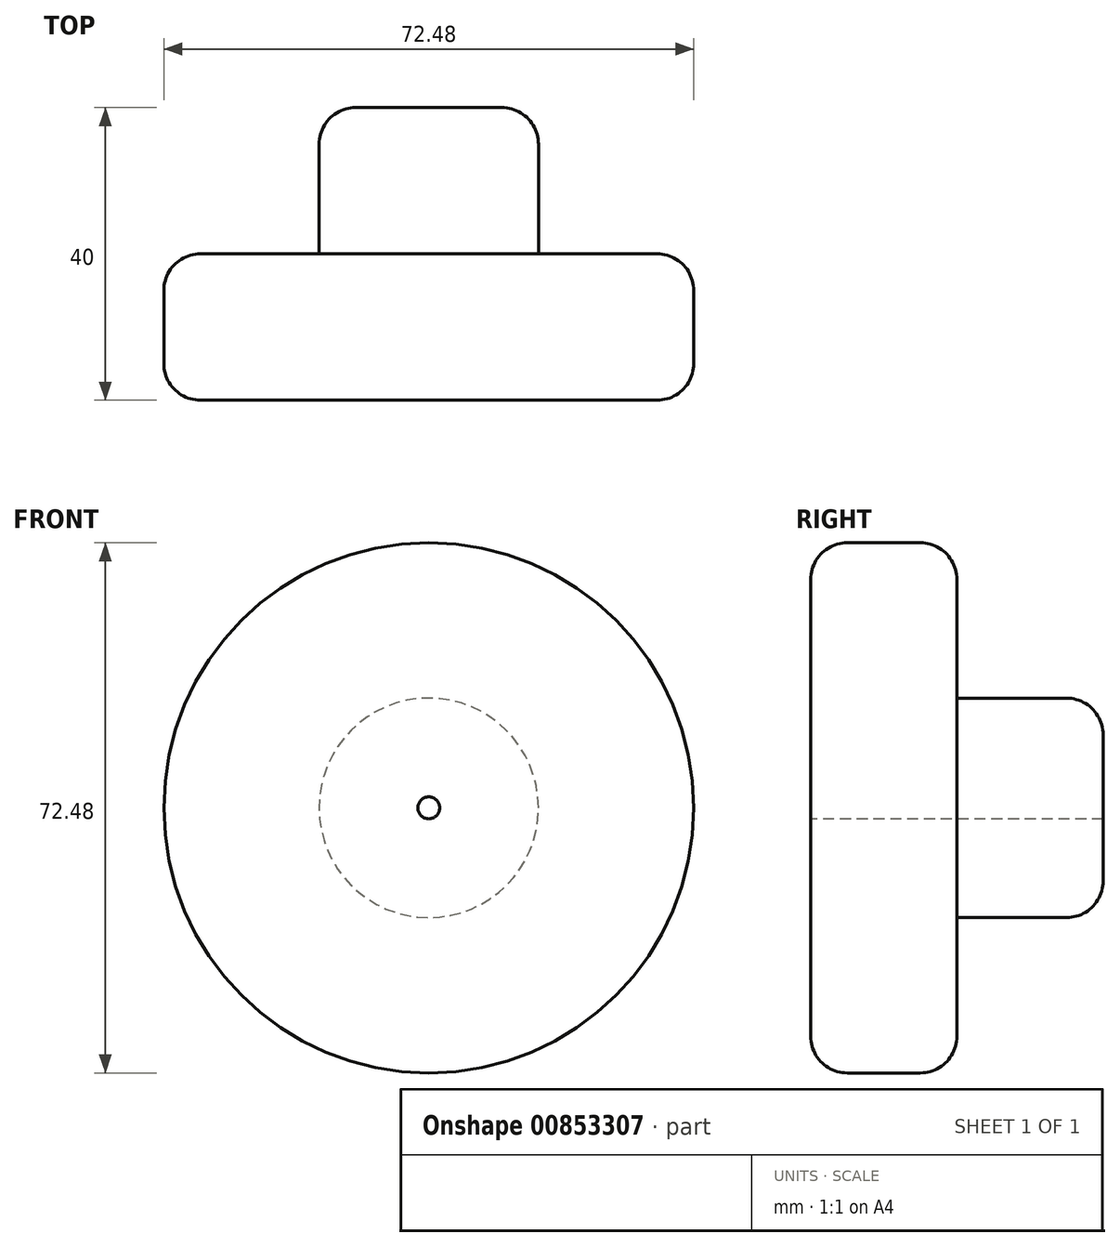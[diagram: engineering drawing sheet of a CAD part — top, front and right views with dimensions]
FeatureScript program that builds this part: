
annotation { "Feature Type Name" : "Feature", "Feature Type Description" : "" }
export const myFeature = defineFeature(function(context is Context, id is Id, definition is map)
    precondition{}
    {
        {
            var Q0;
            Q0=qCreatedBy(makeId("Top.planeOp"),FACE);
            var sketch = newSketch(context, id + "F0", { "sketchPlane" : qUnion([Q0])});
            skLineSegment(sketch, "E0", {"start": v(0, 0) * mm, "end": v(-15, 0) * mm});
            skLineSegment(sketch, "E1", {"start": v(-15, 0) * mm, "end": v(-15, -20) * mm});
            skLineSegment(sketch, "E2", {"start": v(-15, -20) * mm, "end": v(-36.24, -20) * mm});
            skLineSegment(sketch, "E3", {"start": v(-36.24, -20) * mm, "end": v(-36.24, -40) * mm});
            skLineSegment(sketch, "E4", {"start": v(-36.24, -40) * mm, "end": v(0, -40) * mm});
            skLineSegment(sketch, "E5", {"start": v(0, -40) * mm, "end": v(0, 0) * mm});
            skLineSegment(sketch, "E6", {"start": v(0, 30.53) * mm, "end": v(0, -53.97) * mm, "construction": true});
            skSolve(sketch);
        }
        {
            var Q0;
            Q0=makeQuery(id+"F0.imprint","IMPRINT",FACE,{"disambiguationData":[TD([[makeQuery(id+"F0.imprint","IMPRINT",EDGE,{"derivedFrom":sQuery(id+"F0.wireOp",EDGE,"E0")}),1.0]])]});
            var Q1;
            Q1=sQuery(id+"F0.wireOp",EDGE,"E6");
            revolve(context, id + "F1", {"surfaceOperationType" : NewSurfaceOperationType.NEW, "entities" : qUnion([Q0]), "axis" : qUnion([Q1]), "revolveType" : RevolveType.FULL});
        }
        {
            var Q0;
            Q0=makeQuery(id+"F1.opRevolve","SWEPT_EDGE",EDGE,{"disambiguationData":[OSD([sQuery(id+"F0.wireOp",EDGE,"E0"),sQuery(id+"F0.wireOp",EDGE,"E1")])]});
            var Q1;
            Q1=makeQuery(id+"F1.opRevolve","SWEPT_EDGE",EDGE,{"disambiguationData":[OSD([sQuery(id+"F0.wireOp",EDGE,"E2"),sQuery(id+"F0.wireOp",EDGE,"E3")])]});
            var Q2;
            Q2=makeQuery(id+"F1.opRevolve","SWEPT_EDGE",EDGE,{"disambiguationData":[OSD([sQuery(id+"F0.wireOp",EDGE,"E3"),sQuery(id+"F0.wireOp",EDGE,"E4")])]});
            fillet(context, id + "F2", {"entities" : qUnion([Q0, Q1, Q2]), "radius" : 5 * mm, "tangentPropagation" : true, "allowEdgeOverflow" : false});
        }
        {
            var Q0;
            Q0=makeQuery(id+"F1.opRevolve","SWEPT_FACE",FACE,{"disambiguationData":[OSD([sQuery(id+"F0.wireOp",EDGE,"E4")])]});
            var sketch = newSketch(context, id + "F3", { "sketchPlane" : qUnion([Q0])});
            skCircle(sketch, "E7", {"center": v(0, 0) * mm, "radius": 1.5 * mm});
            skSolve(sketch);
        }
        {
            var Q0;
            Q0 = qSketchRegion(id + "F3", true);
            extrude(context, id + "F4", {"entities" : qUnion([Q0]), "operationType" : NewBodyOperationType.REMOVE, "oppositeDirection" : true, "depth" : 70.5 * mm, "offsetDistance" : 25 * mm});
        }
    });
